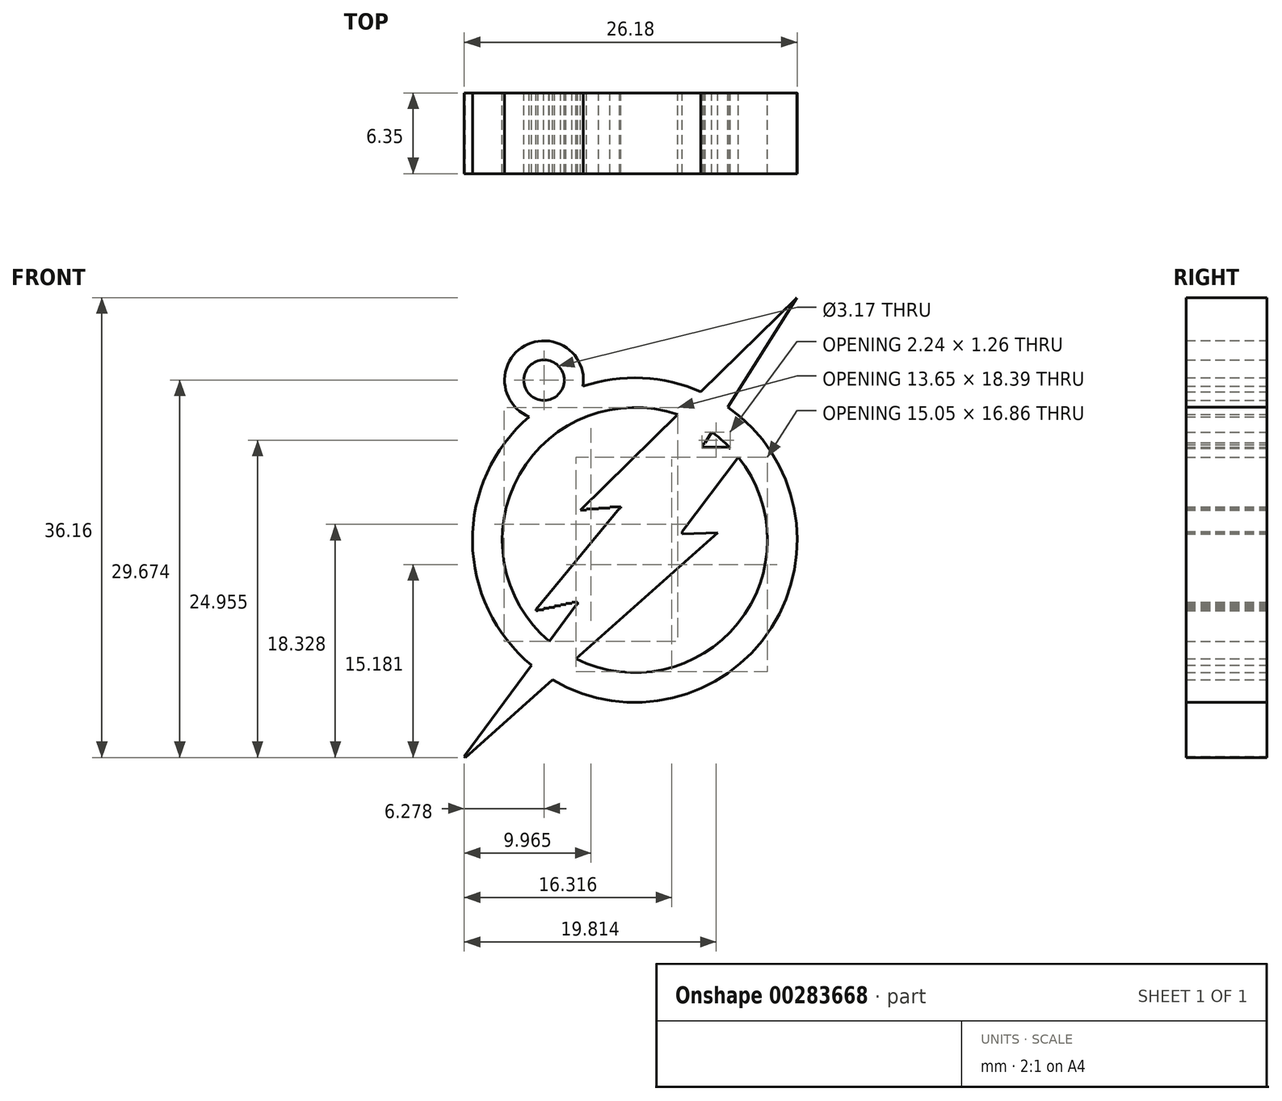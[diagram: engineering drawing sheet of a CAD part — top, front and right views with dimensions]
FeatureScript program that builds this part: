
annotation { "Feature Type Name" : "Feature", "Feature Type Description" : "" }
export const myFeature = defineFeature(function(context is Context, id is Id, definition is map)
    precondition{}
    {
        {
            var Q0;
            Q0=qCreatedBy(makeId("Front.planeOp"),FACE);
            var sketch = newSketch(context, id + "F0", { "sketchPlane" : qUnion([Q0])});
            skLineSegment(sketch, "E0", {"start": v(32.33, 37.52) * mm, "end": v(15.32, 20.8) * mm});
            skLineSegment(sketch, "E1", {"start": v(15.32, 20.8) * mm, "end": v(15.8, 20.8) * mm});
            skLineSegment(sketch, "E2", {"start": v(15.8, 20.8) * mm, "end": v(15.8, 20.9) * mm});
            skLineSegment(sketch, "E3", {"start": v(15.8, 20.9) * mm, "end": v(16.76, 20.9) * mm});
            skLineSegment(sketch, "E4", {"start": v(16.76, 20.9) * mm, "end": v(16.76, 20.98) * mm});
            skLineSegment(sketch, "E5", {"start": v(16.76, 20.98) * mm, "end": v(17.63, 20.98) * mm});
            skLineSegment(sketch, "E6", {"start": v(17.63, 20.98) * mm, "end": v(17.63, 21.06) * mm});
            skLineSegment(sketch, "E7", {"start": v(17.63, 21.06) * mm, "end": v(18.5, 21.06) * mm});
            skLineSegment(sketch, "E8", {"start": v(18.5, 21.06) * mm, "end": v(18.5, 20.98) * mm});
            skLineSegment(sketch, "E9", {"start": v(18.5, 20.98) * mm, "end": v(18.38, 20.98) * mm});
            skLineSegment(sketch, "E10", {"start": v(18.38, 20.98) * mm, "end": v(11.84, 13.01) * mm});
            skLineSegment(sketch, "E11", {"start": v(11.84, 13.01) * mm, "end": v(11.84, 12.9) * mm});
            skLineSegment(sketch, "E12", {"start": v(11.84, 12.9) * mm, "end": v(12, 12.9) * mm});
            skLineSegment(sketch, "E13", {"start": v(12, 12.9) * mm, "end": v(12, 12.98) * mm});
            skLineSegment(sketch, "E14", {"start": v(12, 12.98) * mm, "end": v(12.43, 12.98) * mm});
            skLineSegment(sketch, "E15", {"start": v(12.43, 12.98) * mm, "end": v(12.43, 13.08) * mm});
            skLineSegment(sketch, "E16", {"start": v(12.43, 13.08) * mm, "end": v(12.85, 13.08) * mm});
            skLineSegment(sketch, "E17", {"start": v(12.85, 13.08) * mm, "end": v(12.85, 13.17) * mm});
            skLineSegment(sketch, "E18", {"start": v(12.85, 13.17) * mm, "end": v(13.3, 13.17) * mm});
            skLineSegment(sketch, "E19", {"start": v(13.3, 13.17) * mm, "end": v(13.3, 13.29) * mm});
            skLineSegment(sketch, "E20", {"start": v(13.3, 13.29) * mm, "end": v(13.76, 13.29) * mm});
            skLineSegment(sketch, "E21", {"start": v(13.76, 13.29) * mm, "end": v(13.76, 13.37) * mm});
            skLineSegment(sketch, "E22", {"start": v(13.76, 13.37) * mm, "end": v(14.19, 13.37) * mm});
            skLineSegment(sketch, "E23", {"start": v(14.19, 13.37) * mm, "end": v(14.19, 13.46) * mm});
            skLineSegment(sketch, "E24", {"start": v(14.19, 13.46) * mm, "end": v(14.64, 13.46) * mm});
            skLineSegment(sketch, "E25", {"start": v(14.64, 13.46) * mm, "end": v(14.64, 13.58) * mm});
            skLineSegment(sketch, "E26", {"start": v(14.64, 13.58) * mm, "end": v(15.09, 13.58) * mm});
            skLineSegment(sketch, "E27", {"start": v(15.09, 13.58) * mm, "end": v(15.09, 13.37) * mm});
            skLineSegment(sketch, "E28", {"start": v(15.09, 13.37) * mm, "end": v(15, 13.37) * mm});
            skLineSegment(sketch, "E29", {"start": v(15, 13.37) * mm, "end": v(6.18, 1.44) * mm});
            skLineSegment(sketch, "E30", {"start": v(6.18, 1.44) * mm, "end": v(6.28, 1.36) * mm});
            skLineSegment(sketch, "E31", {"start": v(6.28, 1.36) * mm, "end": v(26.1, 19.04) * mm});
            skLineSegment(sketch, "E32", {"start": v(26.1, 19.04) * mm, "end": v(23.33, 18.93) * mm});
            skLineSegment(sketch, "E33", {"start": v(23.33, 18.93) * mm, "end": v(23.32, 19.13) * mm});
            skLineSegment(sketch, "E34", {"start": v(23.32, 19.13) * mm, "end": v(28.19, 25.57) * mm});
            skLineSegment(sketch, "E35", {"start": v(28.19, 25.57) * mm, "end": v(28.19, 25.68) * mm});
            skLineSegment(sketch, "E36", {"start": v(28.19, 25.68) * mm, "end": v(27, 25.68) * mm});
            skLineSegment(sketch, "E37", {"start": v(27, 25.68) * mm, "end": v(27, 25.75) * mm});
            skLineSegment(sketch, "E38", {"start": v(27, 25.75) * mm, "end": v(24.88, 25.75) * mm});
            skLineSegment(sketch, "E39", {"start": v(24.88, 25.75) * mm, "end": v(24.88, 25.78) * mm});
            skLineSegment(sketch, "E40", {"start": v(24.88, 25.78) * mm, "end": v(24.93, 25.78) * mm});
            skLineSegment(sketch, "E41", {"start": v(24.93, 25.78) * mm, "end": v(24.93, 25.97) * mm});
            skLineSegment(sketch, "E42", {"start": v(24.93, 25.97) * mm, "end": v(25.03, 25.96) * mm});
            skLineSegment(sketch, "E43", {"start": v(25.03, 25.96) * mm, "end": v(25.03, 26.12) * mm});
            skLineSegment(sketch, "E44", {"start": v(25.03, 26.12) * mm, "end": v(25.13, 26.12) * mm});
            skLineSegment(sketch, "E45", {"start": v(25.13, 26.12) * mm, "end": v(32.33, 37.52) * mm});
            skSolve(sketch);
        }
        {
            var Q0;
            Q0=qCreatedBy(makeId("Front.planeOp"),FACE);
            var sketch = newSketch(context, id + "F1", { "sketchPlane" : qUnion([Q0])});
            skArc(sketch, "E46", {"start": v(11.3, 28.16) * mm, "mid": v(25.9, 7.36) * mm, "end": v(15.52, 30.55) * mm});
            skCircle(sketch, "E47", {"center": v(19.6, 18.46) * mm, "radius": 10.43 * mm});
            skArc(sketch, "E48", {"start": v(15.52, 30.55) * mm, "mid": v(10.93, 33.73) * mm, "end": v(11.3, 28.16) * mm});
            skCircle(sketch, "E49", {"center": v(12.46, 31.03) * mm, "radius": 1.59 * mm});
            skSolve(sketch);
        }
        {
            var Q0;
            Q0=makeQuery(id+"F1.imprint","IMPRINT",FACE,{"disambiguationData":[TD([[makeQuery(id+"F1.imprint","IMPRINT",EDGE,{"derivedFrom":sQuery(id+"F1.wireOp",EDGE,"E46")}),1.0]])]});
            extrude(context, id + "F2", {"entities" : qUnion([Q0]), "depth" : 6.35 * mm});
        }
        {
            var Q0;
            Q0 = qSketchRegion(id + "F0", true);
            extrude(context, id + "F3", {"entities" : qUnion([Q0]), "operationType" : NewBodyOperationType.ADD, "depth" : 6.35 * mm});
        }
    });
